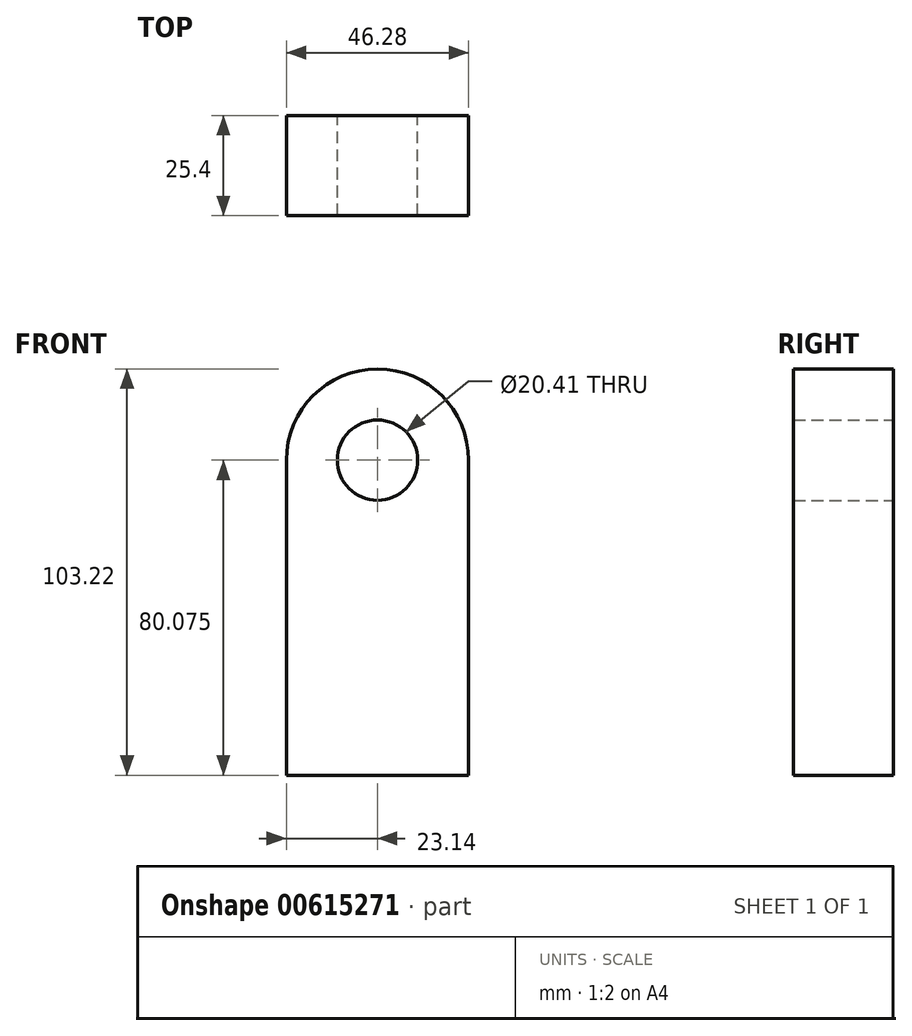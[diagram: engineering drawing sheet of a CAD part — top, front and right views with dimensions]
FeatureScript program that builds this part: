
annotation { "Feature Type Name" : "Feature", "Feature Type Description" : "" }
export const myFeature = defineFeature(function(context is Context, id is Id, definition is map)
    precondition{}
    {
        {
            var Q0;
            Q0=qCreatedBy(makeId("Front.planeOp"),FACE);
            var sketch = newSketch(context, id + "F0", { "sketchPlane" : qUnion([Q0])});
            skLineSegment(sketch, "E0.top", {"start": v(-23.14, -40.04) * mm, "end": v(23.14, -40.04) * mm});
            skLineSegment(sketch, "E0.left", {"start": v(-23.14, 40.04) * mm, "end": v(-23.14, -40.04) * mm});
            skLineSegment(sketch, "E0.right", {"start": v(23.14, 40.04) * mm, "end": v(23.14, -40.04) * mm});
            skPoint(sketch, "E0.middle", {"position": v(0, 0) * mm});
            skArc(sketch, "E1", {"start": v(23.14, 40.04) * mm, "mid": v(0, 63.18) * mm, "end": v(-23.14, 40.04) * mm});
            skCircle(sketch, "E2", {"center": v(0, 40.04) * mm, "radius": 10.2 * mm});
            skSolve(sketch);
        }
        {
            var Q0;
            Q0 = qSketchRegion(id + "F0", true);
            extrude(context, id + "F1", {"entities" : qUnion([Q0]), "depth" : 25.4 * mm, "offsetDistance" : 25.4 * mm});
        }
    });
